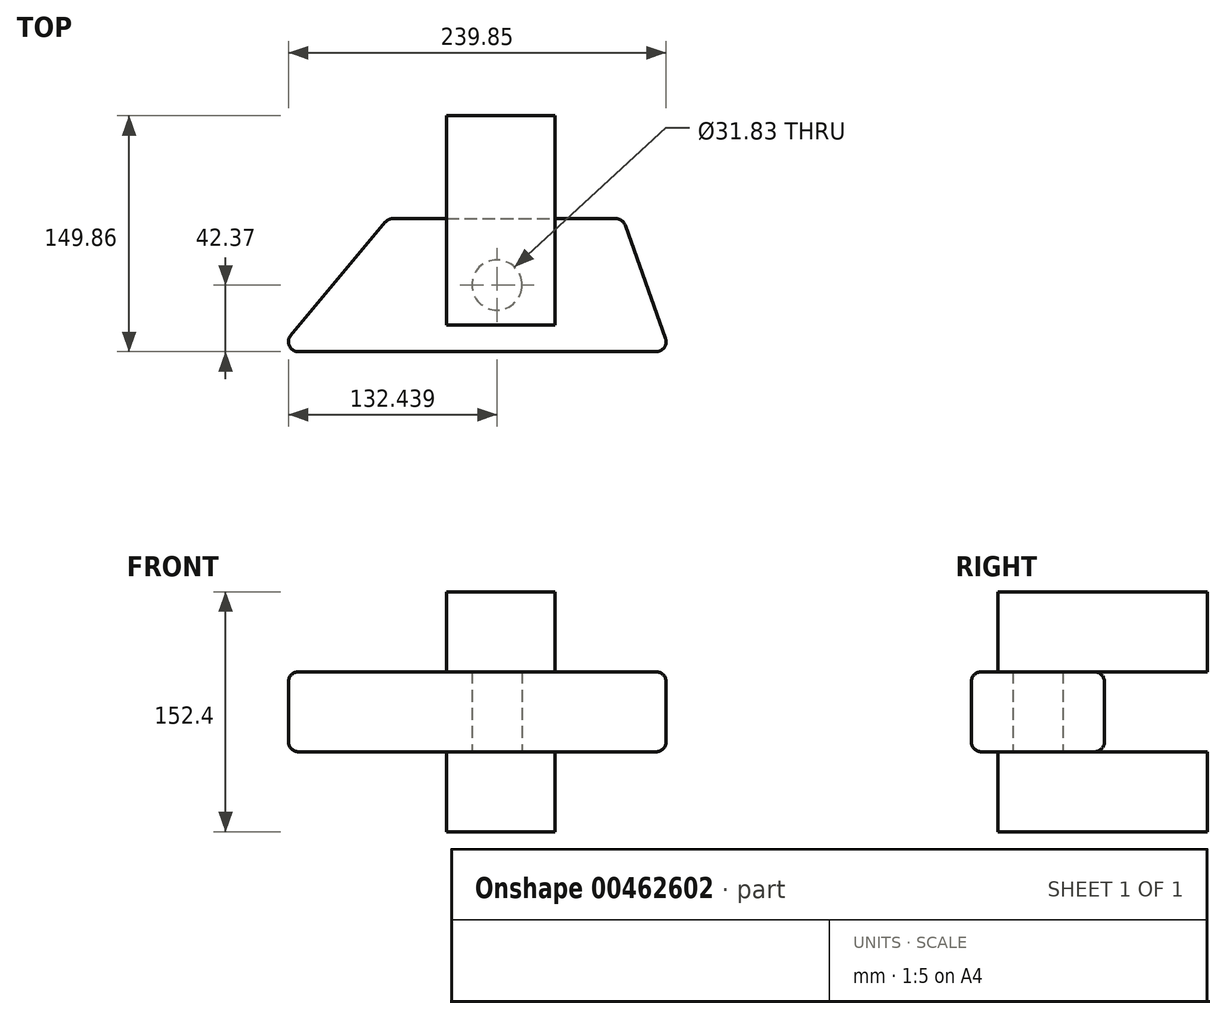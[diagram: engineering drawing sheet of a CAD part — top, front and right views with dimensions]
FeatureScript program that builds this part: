
annotation { "Feature Type Name" : "Feature", "Feature Type Description" : "" }
export const myFeature = defineFeature(function(context is Context, id is Id, definition is map)
    precondition{}
    {
        {
            var Q0;
            Q0=qCreatedBy(makeId("Top.planeOp"),FACE);
            var sketch = newSketch(context, id + "F0", { "sketchPlane" : qUnion([Q0])});
            skLineSegment(sketch, "E0", {"start": v(-110.25, -57.15) * mm, "end": v(-39.65, 27.35) * mm});
            skLineSegment(sketch, "E1", {"start": v(-39.65, 27.35) * mm, "end": v(109.39, 27.35) * mm});
            skLineSegment(sketch, "E2", {"start": v(109.39, 27.35) * mm, "end": v(139.48, -57.15) * mm});
            skLineSegment(sketch, "E3", {"start": v(139.48, -57.15) * mm, "end": v(-110.25, -57.15) * mm});
            skSolve(sketch);
        }
        {
            var Q0;
            Q0 = qSketchRegion(id + "F0", true);
            extrude(context, id + "F1", {"entities" : qUnion([Q0]), "endBound" : BoundingType.SYMMETRIC, "depth" : 50.8 * mm});
        }
        {
            var Q0;
            Q0=makeQuery(id+"F1.opExtrude","SWEPT_FACE",FACE,{"disambiguationData":[OSD([sQuery(id+"F0.wireOp",EDGE,"E1")])]});
            var Q1;
            Q1=makeQuery(id+"F1.opExtrude","SWEPT_FACE",FACE,{"disambiguationData":[OSD([sQuery(id+"F0.wireOp",EDGE,"E0")])]});
            var Q2;
            Q2=makeQuery(id+"F1.opExtrude","SWEPT_FACE",FACE,{"disambiguationData":[OSD([sQuery(id+"F0.wireOp",EDGE,"E2")])]});
            var Q3;
            Q3=makeQuery(id+"F1.opExtrude","CAP_FACE",FACE,{"disambiguationData":[OSD([sQuery(id+"F0.wireOp",EDGE,"E0"),sQuery(id+"F0.wireOp",EDGE,"E1"),sQuery(id+"F0.wireOp",EDGE,"E2"),sQuery(id+"F0.wireOp",EDGE,"E3")])],"isStart":true});
            var Q4;
            Q4=makeQuery(id+"F1.opExtrude","SWEPT_FACE",FACE,{"disambiguationData":[OSD([sQuery(id+"F0.wireOp",EDGE,"E3")])]});
            fillet(context, id + "F2", {"entities" : qUnion([Q0, Q1, Q2, Q3, Q4]), "radius" : 6.35 * mm, "tangentPropagation" : true, "allowEdgeOverflow" : false});
        }
        {
            var Q0;
            Q0=makeQuery(id+"F1.opExtrude","CAP_FACE",FACE,{"disambiguationData":[OSD([sQuery(id+"F0.wireOp",EDGE,"E0"),sQuery(id+"F0.wireOp",EDGE,"E1"),sQuery(id+"F0.wireOp",EDGE,"E2"),sQuery(id+"F0.wireOp",EDGE,"E3")])],"isStart":false});
            var sketch = newSketch(context, id + "F3", { "sketchPlane" : qUnion([Q0])});
            skCircle(sketch, "E4", {"center": v(29.42, -14.78) * mm, "radius": 15.91 * mm});
            skSolve(sketch);
        }
        {
            var Q0;
            Q0 = qSketchRegion(id + "F3", true);
            extrude(context, id + "F4", {"entities" : qUnion([Q0]), "operationType" : NewBodyOperationType.REMOVE, "endBound" : BoundingType.THROUGH_ALL, "oppositeDirection" : true, "depth" : 25.4 * mm});
        }
        {
            var Q0;
            Q0=makeQuery(id+"F1.opExtrude","CAP_FACE",FACE,{"disambiguationData":[OSD([sQuery(id+"F0.wireOp",EDGE,"E0"),sQuery(id+"F0.wireOp",EDGE,"E1"),sQuery(id+"F0.wireOp",EDGE,"E2"),sQuery(id+"F0.wireOp",EDGE,"E3")])],"isStart":false});
            var sketch = newSketch(context, id + "F5", { "sketchPlane" : qUnion([Q0])});
            skLineSegment(sketch, "E5.bottom", {"start": v(-2.73, 92.7) * mm, "end": v(66.23, 92.7) * mm});
            skLineSegment(sketch, "E5.top", {"start": v(-2.73, -40.3) * mm, "end": v(66.23, -40.3) * mm});
            skLineSegment(sketch, "E5.left", {"start": v(-2.73, 92.7) * mm, "end": v(-2.73, -40.3) * mm});
            skLineSegment(sketch, "E5.right", {"start": v(66.23, 92.7) * mm, "end": v(66.23, -40.3) * mm});
            skSolve(sketch);
        }
        {
            var Q0;
            Q0 = qSketchRegion(id + "F5", true);
            extrude(context, id + "F6", {"entities" : qUnion([Q0]), "depth" : 50.8 * mm});
        }
        {
            var Q0;
            Q0=makeQuery(id+"F6.opExtrude","SWEPT_BODY",BODY,{"disambiguationData":[OSD([sQuery(id+"F5.wireOp",EDGE,"E5.bottom"),sQuery(id+"F5.wireOp",EDGE,"E5.top"),sQuery(id+"F5.wireOp",EDGE,"E5.left"),sQuery(id+"F5.wireOp",EDGE,"E5.right")])]});
            var Q1;
            Q1=qCreatedBy(makeId("Top.planeOp"),FACE);
            mirror(context, id + "F7", {"entities" : qUnion([Q0]), "mirrorPlane" : qUnion([Q1])});
        }
        {
            var Q0;
            {var subQ0=sQuery(id+"F5.wireOp",EDGE,"E5.left");var subQ2=sQuery(id+"F5.wireOp",EDGE,"E5.bottom");var subQ3=sQuery(id+"F5.wireOp",EDGE,"E5.right");Q0=makeQuery(id+"F7.boolean.opBoolean","SPLIT",FACE,{"disambiguationData":[TD([makeQuery(id+"F7.opPattern","COPY",FACE,{"derivedFrom":makeQuery(id+"F6.opExtrude","SWEPT_FACE",FACE,{"disambiguationData":[OSD([subQ2])]}),"instanceName":"1"})])],"derivedFrom":makeQuery(id+"F7.opPattern","COPY",FACE,{"derivedFrom":makeQuery(id+"F6.opExtrude","CAP_FACE",FACE,{"disambiguationData":[OSD([subQ2,sQuery(id+"F5.wireOp",EDGE,"E5.top"),subQ0,subQ3])],"isStart":true}),"instanceName":"1"})});}
            var sketch = newSketch(context, id + "F8", { "sketchPlane" : qUnion([Q0])});
            skCircle(sketch, "E6.0", {"center": v(29.42, -14.78) * mm, "radius": 15.91 * mm});
            skSolve(sketch);
        }
        {
            var Q0;
            Q0 = qSketchRegion(id + "F8", true);
            var Q1;
            {var subQ0=sQuery(id+"F5.wireOp",EDGE,"E5.bottom");var subQ2=sQuery(id+"F5.wireOp",EDGE,"E5.left");var subQ3=sQuery(id+"F5.wireOp",EDGE,"E5.right");Q1=makeQuery(id+"F7.boolean.opBoolean","SPLIT",FACE,{"disambiguationData":[TD([makeQuery(id+"F6.opExtrude","SWEPT_FACE",FACE,{"disambiguationData":[OSD([subQ0])]})])],"derivedFrom":makeQuery(id+"F6.opExtrude","CAP_FACE",FACE,{"disambiguationData":[OSD([subQ0,sQuery(id+"F5.wireOp",EDGE,"E5.top"),subQ2,subQ3])],"isStart":true})});}
            extrude(context, id + "F9", {"entities" : qUnion([Q0]), "endBound" : BoundingType.UP_TO_SURFACE, "endBoundEntityFace" : qUnion([Q1]), "depth" : 25.4 * mm});
        }
    });
